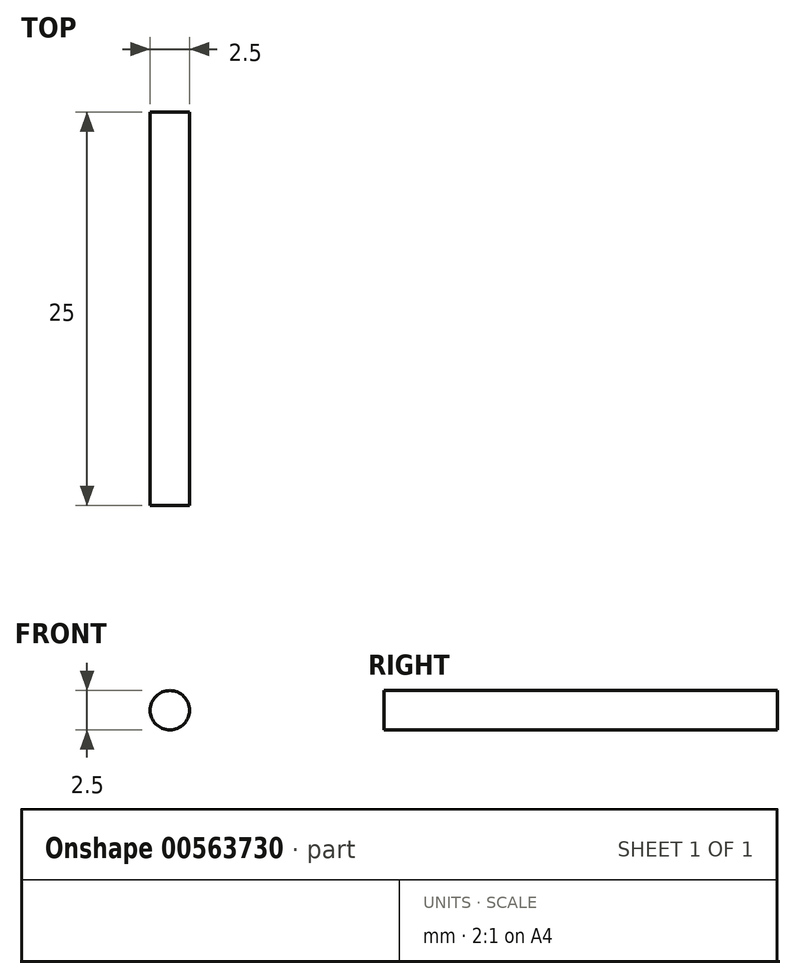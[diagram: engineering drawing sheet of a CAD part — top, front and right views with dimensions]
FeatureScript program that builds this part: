
annotation { "Feature Type Name" : "Feature", "Feature Type Description" : "" }
export const myFeature = defineFeature(function(context is Context, id is Id, definition is map)
    precondition{}
    {
        {
            var Q0;
            Q0=qCreatedBy(makeId("Front.planeOp"),FACE);
            var sketch = newSketch(context, id + "F0", { "sketchPlane" : qUnion([Q0])});
            skCircle(sketch, "E0", {"center": v(0, 0) * mm, "radius": 1.25 * mm});
            skArc(sketch, "E1", {"start": v(1.09, -1.03) * mm, "mid": v(0, 1.5) * mm, "end": v(-1.09, -1.03) * mm});
            skLineSegment(sketch, "E2", {"start": v(0.58, -1.25) * mm, "end": v(-0.58, -1.25) * mm});
            skPoint(sketch, "E3.visualSharp", {"position": v(-0.83, -1.25) * mm});
            skArc(sketch, "E3.filletArc", {"start": v(-1.09, -1.03) * mm, "mid": v(-0.86, -1.2) * mm, "end": v(-0.58, -1.25) * mm});
            skPoint(sketch, "E4.visualSharp", {"position": v(0.83, -1.25) * mm});
            skArc(sketch, "E4.filletArc", {"start": v(0.58, -1.25) * mm, "mid": v(0.86, -1.2) * mm, "end": v(1.09, -1.03) * mm});
            skSolve(sketch);
        }
        {
            var Q0;
            Q0=makeQuery(id+"F0.imprint","IMPRINT",FACE,{"disambiguationData":[TD([[makeQuery(id+"F0.imprint","IMPRINT",EDGE,{"derivedFrom":sQuery(id+"F0.wireOp",EDGE,"E0")}),1.0]])]});
            extrude(context, id + "F1", {"entities" : qUnion([Q0]), "depth" : 25 * mm, "offsetDistance" : 25 * mm});
        }
    });
